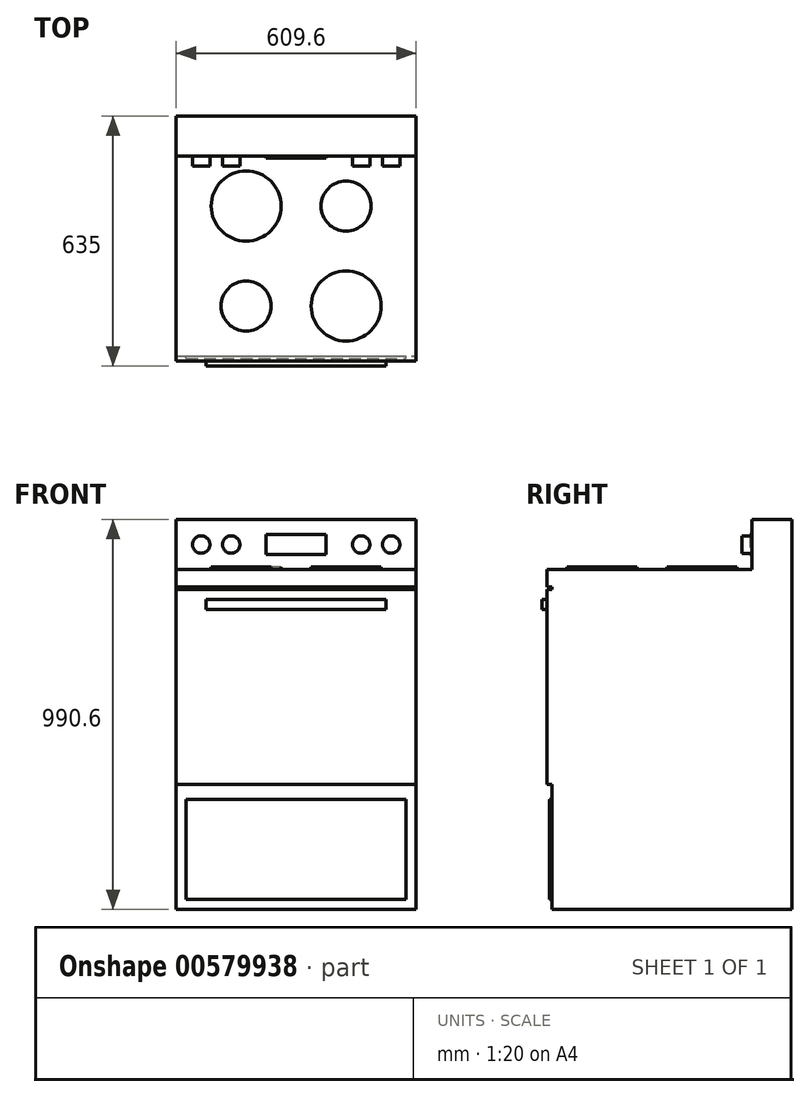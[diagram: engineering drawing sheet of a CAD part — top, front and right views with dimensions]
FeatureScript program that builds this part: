
annotation { "Feature Type Name" : "Feature", "Feature Type Description" : "" }
export const myFeature = defineFeature(function(context is Context, id is Id, definition is map)
    precondition{}
    {
        {
            var Q0;
            Q0=qCreatedBy(makeId("Front.planeOp"),FACE);
            var sketch = newSketch(context, id + "F0", { "sketchPlane" : qUnion([Q0])});
            skLineSegment(sketch, "E0.bottom", {"start": v(-392.55, 441.93) * mm, "end": v(217.05, 441.93) * mm});
            skLineSegment(sketch, "E0.top", {"start": v(-392.55, -421.67) * mm, "end": v(217.05, -421.67) * mm});
            skLineSegment(sketch, "E0.left", {"start": v(-392.55, 441.93) * mm, "end": v(-392.55, -421.67) * mm});
            skLineSegment(sketch, "E0.right", {"start": v(217.05, 441.93) * mm, "end": v(217.05, -421.67) * mm});
            skSolve(sketch);
        }
        {
            var Q0;
            Q0=makeQuery(id+"F0.imprint","IMPRINT",FACE,{"disambiguationData":[TD([[makeQuery(id+"F0.imprint","IMPRINT",EDGE,{"derivedFrom":sQuery(id+"F0.wireOp",EDGE,"E0.bottom")}),-1.0]])]});
            extrude(context, id + "F1", {"entities" : qUnion([Q0]), "depth" : 609.6 * mm, "offsetDistance" : 25.4 * mm});
        }
        {
            var Q0;
            Q0=makeQuery(id+"F1.opExtrude","SWEPT_FACE",FACE,{"disambiguationData":[OSD([sQuery(id+"F0.wireOp",EDGE,"E0.bottom")])]});
            var sketch = newSketch(context, id + "F2", { "sketchPlane" : qUnion([Q0])});
            skLineSegment(sketch, "E1.bottom", {"start": v(-392.55, 0) * mm, "end": v(217.05, 0) * mm});
            skLineSegment(sketch, "E1.top", {"start": v(-392.55, -101.6) * mm, "end": v(217.05, -101.6) * mm});
            skLineSegment(sketch, "E1.left", {"start": v(-392.55, 0) * mm, "end": v(-392.55, -101.6) * mm});
            skLineSegment(sketch, "E1.right", {"start": v(217.05, 0) * mm, "end": v(217.05, -101.6) * mm});
            skSolve(sketch);
        }
        {
            var Q0;
            Q0=makeQuery(id+"F2.imprint","IMPRINT",FACE,{"disambiguationData":[TD([[makeQuery(id+"F2.imprint","IMPRINT",EDGE,{"derivedFrom":sQuery(id+"F2.wireOp",EDGE,"E1.bottom")}),-1.0]])]});
            extrude(context, id + "F3", {"entities" : qUnion([Q0]), "operationType" : NewBodyOperationType.ADD, "depth" : 127 * mm, "offsetDistance" : 25.4 * mm});
        }
        {
            var Q0;
            Q0=makeQuery(id+"F1.opExtrude","SWEPT_FACE",FACE,{"disambiguationData":[OSD([sQuery(id+"F0.wireOp",EDGE,"E0.bottom")])]});
            var sketch = newSketch(context, id + "F4", { "sketchPlane" : qUnion([Q0])});
            skCircle(sketch, "E2", {"center": v(-214.75, -228.6) * mm, "radius": 88.9 * mm});
            skCircle(sketch, "E3", {"center": v(-214.75, -482.6) * mm, "radius": 63.5 * mm});
            skCircle(sketch, "E4", {"center": v(39.25, -482.6) * mm, "radius": 88.9 * mm});
            skCircle(sketch, "E5", {"center": v(39.25, -228.6) * mm, "radius": 63.5 * mm});
            skSolve(sketch);
        }
        {
            var Q0;
            Q0 = qSketchRegion(id + "F4", true);
            extrude(context, id + "F5", {"entities" : qUnion([Q0]), "operationType" : NewBodyOperationType.ADD, "depth" : 6.35 * mm, "offsetDistance" : 25.4 * mm});
        }
        {
            var Q0;
            Q0=makeQuery(id+"F1.opExtrude","CAP_FACE",FACE,{"disambiguationData":[OSD([sQuery(id+"F0.wireOp",EDGE,"E0.bottom"),sQuery(id+"F0.wireOp",EDGE,"E0.top"),sQuery(id+"F0.wireOp",EDGE,"E0.left"),sQuery(id+"F0.wireOp",EDGE,"E0.right")])],"isStart":false});
            var sketch = newSketch(context, id + "F6", { "sketchPlane" : qUnion([Q0])});
            skLineSegment(sketch, "E6.bottom", {"start": v(-367.15, -142.27) * mm, "end": v(191.65, -142.27) * mm});
            skLineSegment(sketch, "E6.top", {"start": v(-367.15, -396.27) * mm, "end": v(191.65, -396.27) * mm});
            skLineSegment(sketch, "E6.left", {"start": v(-367.15, -142.27) * mm, "end": v(-367.15, -396.27) * mm});
            skLineSegment(sketch, "E6.right", {"start": v(191.65, -142.27) * mm, "end": v(191.65, -396.27) * mm});
            skSolve(sketch);
        }
        {
            var Q0;
            Q0=makeQuery(id+"F6.imprint","IMPRINT",FACE,{"disambiguationData":[TD([[makeQuery(id+"F6.imprint","IMPRINT",EDGE,{"derivedFrom":sQuery(id+"F6.wireOp",EDGE,"E6.bottom")}),-1.0]])]});
            extrude(context, id + "F7", {"entities" : qUnion([Q0]), "operationType" : NewBodyOperationType.ADD, "depth" : 6.35 * mm, "offsetDistance" : 25.4 * mm});
        }
        {
            var Q0;
            Q0=makeQuery(id+"F1.opExtrude","CAP_FACE",FACE,{"disambiguationData":[OSD([sQuery(id+"F0.wireOp",EDGE,"E0.bottom"),sQuery(id+"F0.wireOp",EDGE,"E0.top"),sQuery(id+"F0.wireOp",EDGE,"E0.left"),sQuery(id+"F0.wireOp",EDGE,"E0.right")])],"isStart":false});
            var sketch = newSketch(context, id + "F8", { "sketchPlane" : qUnion([Q0])});
            skLineSegment(sketch, "E7.bottom", {"start": v(-392.55, 441.93) * mm, "end": v(217.05, 441.93) * mm});
            skLineSegment(sketch, "E7.top", {"start": v(-392.55, 391.13) * mm, "end": v(217.05, 391.13) * mm});
            skLineSegment(sketch, "E7.left", {"start": v(-392.55, 441.93) * mm, "end": v(-392.55, 397.48) * mm});
            skLineSegment(sketch, "E7.right", {"start": v(217.05, 441.93) * mm, "end": v(217.05, 391.13) * mm});
            skLineSegment(sketch, "E8.bottom", {"start": v(-392.55, 397.48) * mm, "end": v(217.05, 397.48) * mm});
            skLineSegment(sketch, "E8.top", {"start": v(-392.55, -104.17) * mm, "end": v(217.05, -104.17) * mm});
            skLineSegment(sketch, "E8.left", {"start": v(-392.55, 391.13) * mm, "end": v(-392.55, -104.17) * mm});
            skLineSegment(sketch, "E8.right", {"start": v(217.05, 391.13) * mm, "end": v(217.05, -104.17) * mm});
            skSolve(sketch);
        }
        {
            var Q0;
            Q0 = qSketchRegion(id + "F8", true);
            extrude(context, id + "F9", {"entities" : qUnion([Q0]), "operationType" : NewBodyOperationType.ADD, "depth" : 12.7 * mm, "offsetDistance" : 25.4 * mm});
        }
        {
            var Q0;
            Q0=makeQuery(id+"F9.opExtrude","CAP_FACE",FACE,{"disambiguationData":[OSD([sQuery(id+"F8.wireOp",EDGE,"E7.top"),sQuery(id+"F8.wireOp",EDGE,"E8.top"),sQuery(id+"F8.wireOp",EDGE,"E8.left"),sQuery(id+"F8.wireOp",EDGE,"E8.right")])],"isStart":false});
            var sketch = newSketch(context, id + "F10", { "sketchPlane" : qUnion([Q0])});
            skLineSegment(sketch, "E9.bottom", {"start": v(-316.35, 365.24) * mm, "end": v(140.85, 365.24) * mm});
            skLineSegment(sketch, "E9.top", {"start": v(-316.35, 339.84) * mm, "end": v(140.85, 339.84) * mm});
            skLineSegment(sketch, "E9.left", {"start": v(-316.35, 365.24) * mm, "end": v(-316.35, 339.84) * mm});
            skLineSegment(sketch, "E9.right", {"start": v(140.85, 365.24) * mm, "end": v(140.85, 339.84) * mm});
            skSolve(sketch);
        }
        {
            var Q0;
            Q0 = qSketchRegion(id + "F10", true);
            extrude(context, id + "F11", {"entities" : qUnion([Q0]), "operationType" : NewBodyOperationType.ADD, "depth" : 12.7 * mm, "offsetDistance" : 25.4 * mm});
        }
        {
            var Q0;
            Q0=makeQuery(id+"F3.opExtrude","SWEPT_FACE",FACE,{"disambiguationData":[OSD([sQuery(id+"F2.wireOp",EDGE,"E1.top")])]});
            var sketch = newSketch(context, id + "F12", { "sketchPlane" : qUnion([Q0])});
            skLineSegment(sketch, "E10.bottom", {"start": v(-163.95, 530.83) * mm, "end": v(-11.55, 530.83) * mm});
            skLineSegment(sketch, "E10.top", {"start": v(-163.95, 480.03) * mm, "end": v(-11.55, 480.03) * mm});
            skLineSegment(sketch, "E10.left", {"start": v(-163.95, 530.83) * mm, "end": v(-163.95, 480.03) * mm});
            skLineSegment(sketch, "E10.right", {"start": v(-11.55, 530.83) * mm, "end": v(-11.55, 480.03) * mm});
            skSolve(sketch);
        }
        {
            var Q0;
            Q0 = qSketchRegion(id + "F12", true);
            extrude(context, id + "F13", {"entities" : qUnion([Q0]), "operationType" : NewBodyOperationType.ADD, "depth" : 5.08 * mm, "offsetDistance" : 25.4 * mm});
        }
        {
            var Q0;
            Q0=makeQuery(id+"F3.opExtrude","SWEPT_FACE",FACE,{"disambiguationData":[OSD([sQuery(id+"F2.wireOp",EDGE,"E1.top")])]});
            var sketch = newSketch(context, id + "F14", { "sketchPlane" : qUnion([Q0])});
            skCircle(sketch, "E11", {"center": v(-329.05, 505.43) * mm, "radius": 22.23 * mm});
            skCircle(sketch, "E12", {"center": v(-252.85, 505.43) * mm, "radius": 22.23 * mm});
            skCircle(sketch, "E13", {"center": v(77.35, 505.43) * mm, "radius": 22.23 * mm});
            skCircle(sketch, "E14", {"center": v(153.55, 505.43) * mm, "radius": 22.23 * mm});
            skSolve(sketch);
        }
        {
            var Q0;
            Q0 = qSketchRegion(id + "F14", true);
            extrude(context, id + "F15", {"entities" : qUnion([Q0]), "operationType" : NewBodyOperationType.ADD, "depth" : 25.4 * mm, "offsetDistance" : 25.4 * mm});
        }
    });
